# Revit family: Hammereinsatz Typ 2530 für Staberder ST, BP und OMEX
name_source: partatom
category: Generic Models
revit_build: Autodesk Revit 2015 (Build: 20140606_1530(x64)
units: mm (PartAtom-declared; Revit-internal decimal feet)

## types (2) — shared parameters
Height = 240 mm  [stored 0.787402 ft]
Height 1 = 16 mm
Height 2 = 55 mm  [stored 0.180446 ft]
Height 3 = 111 mm
Height 4 = 8 mm  [stored 0.0262467 ft]
Height 5 = 55 mm  [stored 0.180446 ft]
Manufacturer = OBO Bettermann
Material = Steel
URL = http://www.obo-bettermann.com
Width = 20 mm  [stored 0.0656168 ft]

## per-type parameters (varying)
| type | GTIN | Manufacturer Art.No. | Width 1 | Width 2 |
| 2530 20 | 4012195243557 | 3043401 | 12 mm  [stored 0.0393701 ft] | 7 mm  [stored 0.0229659 ft] |
| 2530 25 | 4012195243618 | 3043452 | 14 mm  [stored 0.0459318 ft] | 8 mm  [stored 0.0262467 ft] |

note: column(s) folded — value = type name in every type: Article Type

note: [stored X ft] marks values corroborated as IEEE doubles in the binary element streams (Revit-internal decimal feet)

## geometry (parser evidence)
native form markers: Sweep x2
no freeform markers — native parametric forms only
